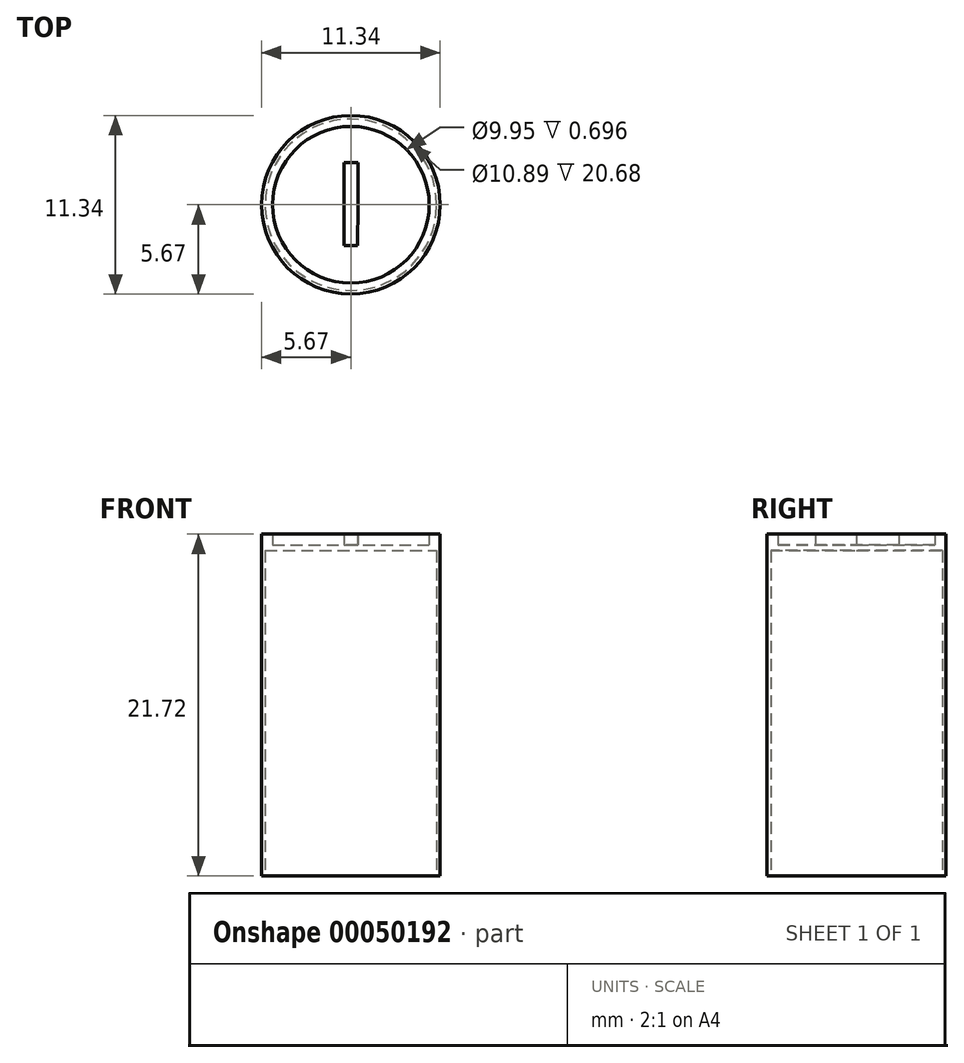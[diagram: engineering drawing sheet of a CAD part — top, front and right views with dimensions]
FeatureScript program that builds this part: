
annotation { "Feature Type Name" : "Feature", "Feature Type Description" : "" }
export const myFeature = defineFeature(function(context is Context, id is Id, definition is map)
    precondition{}
    {
        {
            var Q0;
            Q0=qCreatedBy(makeId("Front.planeOp"),FACE);
            var sketch = newSketch(context, id + "F0", { "sketchPlane" : qUnion([Q0])});
            skLineSegment(sketch, "E0", {"start": v(4.98, 21.02) * mm, "end": v(4.98, 21.72) * mm});
            skLineSegment(sketch, "E1", {"start": v(4.98, 21.72) * mm, "end": v(5.67, 21.72) * mm});
            skLineSegment(sketch, "E2", {"start": v(5.67, 21.72) * mm, "end": v(5.67, 0) * mm});
            skLineSegment(sketch, "E3", {"start": v(5.67, 0) * mm, "end": v(5.44, 0) * mm});
            skLineSegment(sketch, "E4", {"start": v(5.44, 0) * mm, "end": v(5.44, 20.68) * mm});
            skLineSegment(sketch, "E5", {"start": v(5.44, 20.68) * mm, "end": v(0.29, 20.68) * mm});
            skLineSegment(sketch, "E6", {"start": v(4.98, 21.02) * mm, "end": v(0, 21.02) * mm});
            skLineSegment(sketch, "E7", {"start": v(0.29, 20.68) * mm, "end": v(0, 20.68) * mm});
            skLineSegment(sketch, "E8", {"start": v(0, 20.68) * mm, "end": v(0, 21.02) * mm});
            skSolve(sketch);
        }
        {
            var Q0;
            Q0=makeQuery(id+"F0.imprint","IMPRINT",FACE,{"disambiguationData":[TD([[makeQuery(id+"F0.imprint","IMPRINT",EDGE,{"derivedFrom":sQuery(id+"F0.wireOp",EDGE,"E0")}),-1.0]])]});
            var Q1;
            Q1=sQuery(id+"F0.wireOp",EDGE,"E8");
            revolve(context, id + "F1", {"entities" : qUnion([Q0]), "axis" : qUnion([Q1]), "revolveType" : RevolveType.FULL});
        }
        {
            var Q0;
            Q0=makeQuery(id+"F1.opRevolve","SWEPT_FACE",FACE,{"disambiguationData":[OSD([sQuery(id+"F0.wireOp",EDGE,"E6")])]});
            var sketch = newSketch(context, id + "F2", { "sketchPlane" : qUnion([Q0])});
            skLineSegment(sketch, "E9", {"start": v(0.45, 0) * mm, "end": v(0.45, 2.69) * mm});
            skLineSegment(sketch, "E10", {"start": v(0.45, 2.69) * mm, "end": v(-0.42, 2.69) * mm});
            skLineSegment(sketch, "E11", {"start": v(-0.42, 2.69) * mm, "end": v(-0.42, -2.6) * mm});
            skLineSegment(sketch, "E12", {"start": v(-0.42, -2.6) * mm, "end": v(0.41, -2.6) * mm});
            skLineSegment(sketch, "E13", {"start": v(0.41, -2.6) * mm, "end": v(0.45, 0) * mm});
            skSolve(sketch);
        }
        {
            var Q0;
            Q0=makeQuery(id+"F2.imprint","IMPRINT",FACE,{"disambiguationData":[TD([[makeQuery(id+"F2.imprint","IMPRINT",EDGE,{"derivedFrom":sQuery(id+"F2.wireOp",EDGE,"E9")}),1.0]])]});
            extrude(context, id + "F3", {"entities" : qUnion([Q0]), "operationType" : NewBodyOperationType.ADD, "depth" : 0.69 * mm});
        }
    });
